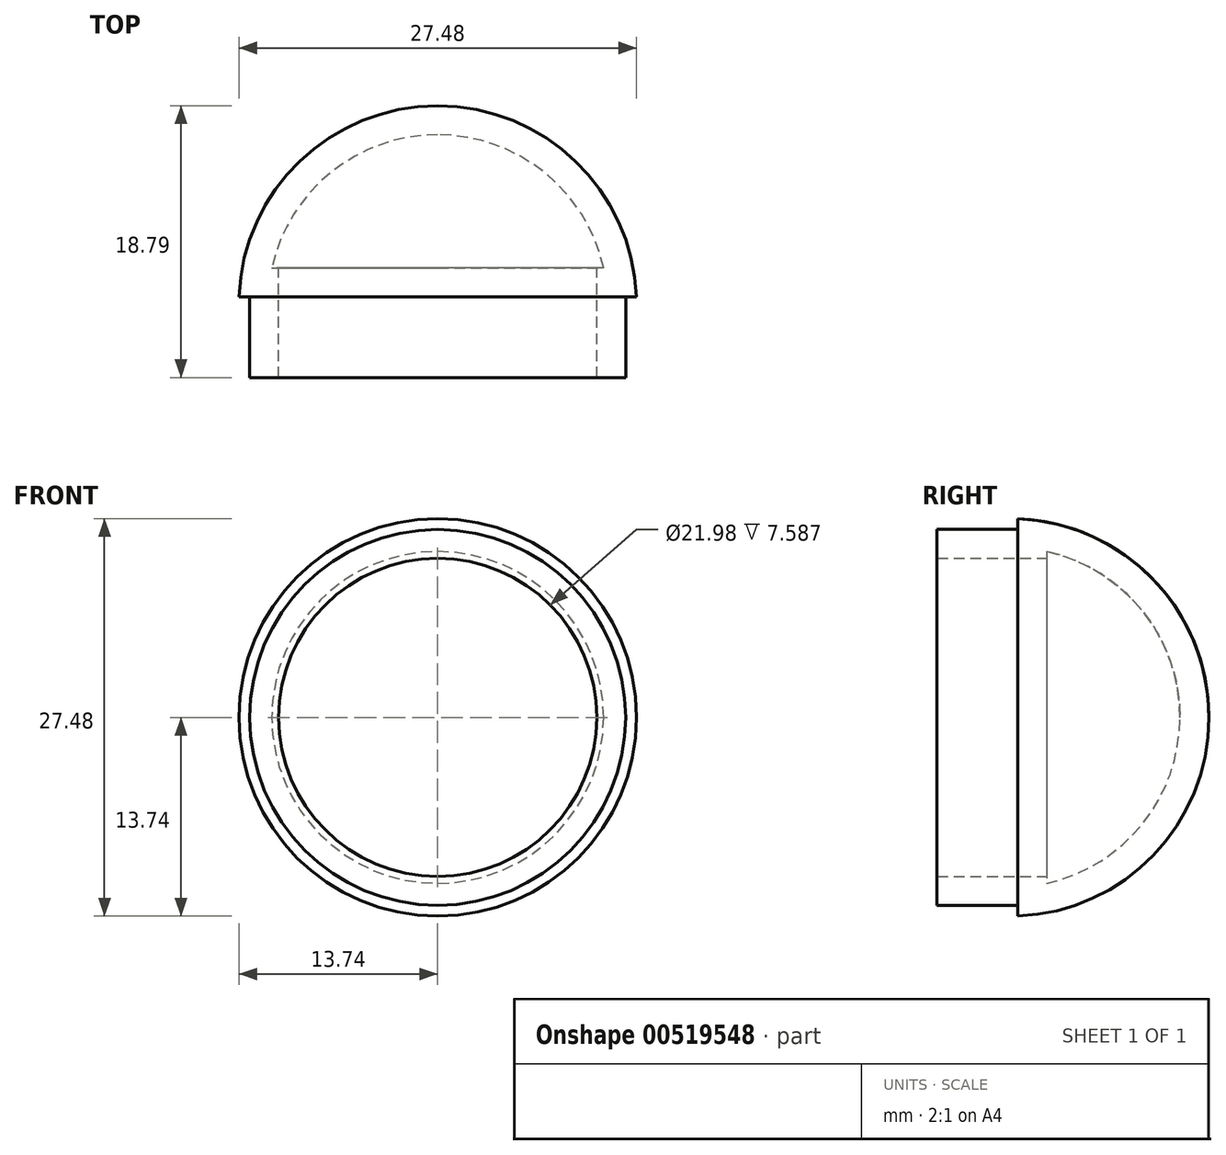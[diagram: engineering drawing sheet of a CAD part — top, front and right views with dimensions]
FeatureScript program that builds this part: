
annotation { "Feature Type Name" : "Feature", "Feature Type Description" : "" }
export const myFeature = defineFeature(function(context is Context, id is Id, definition is map)
    precondition{}
    {
        {
            var Q0;
            Q0=qCreatedBy(makeId("Right.planeOp"),FACE);
            var sketch = newSketch(context, id + "F0", { "sketchPlane" : qUnion([Q0])});
            skLineSegment(sketch, "E0", {"start": v(0, 13) * mm, "end": v(5.59, 13) * mm});
            skLineSegment(sketch, "E1", {"start": v(5.59, 13) * mm, "end": v(5.59, 13.74) * mm});
            skArc(sketch, "E2", {"start": v(18.79, 0) * mm, "mid": v(14.95, 9.52) * mm, "end": v(5.59, 13.74) * mm});
            skLineSegment(sketch, "E3", {"start": v(18.79, 0) * mm, "end": v(0, 0) * mm});
            skLineSegment(sketch, "E4", {"start": v(0, 13) * mm, "end": v(0, 0) * mm});
            skSolve(sketch);
        }
        {
            var Q0;
            Q0 = qSketchRegion(id + "F0", true);
            var Q1;
            Q1=sQuery(id+"F0.wireOp",EDGE,"E3");
            revolve(context, id + "F1", {"entities" : qUnion([Q0]), "axis" : qUnion([Q1]), "revolveType" : RevolveType.FULL});
        }
        {
            var Q0;
            Q0=makeQuery(id+"F1.opRevolve","SWEPT_FACE",FACE,{"disambiguationData":[OSD([sQuery(id+"F0.wireOp",EDGE,"E4")])]});
            shell(context, id + "F2", {"entities" : qUnion([Q0]), "thickness" : 2 * mm});
        }
    });
